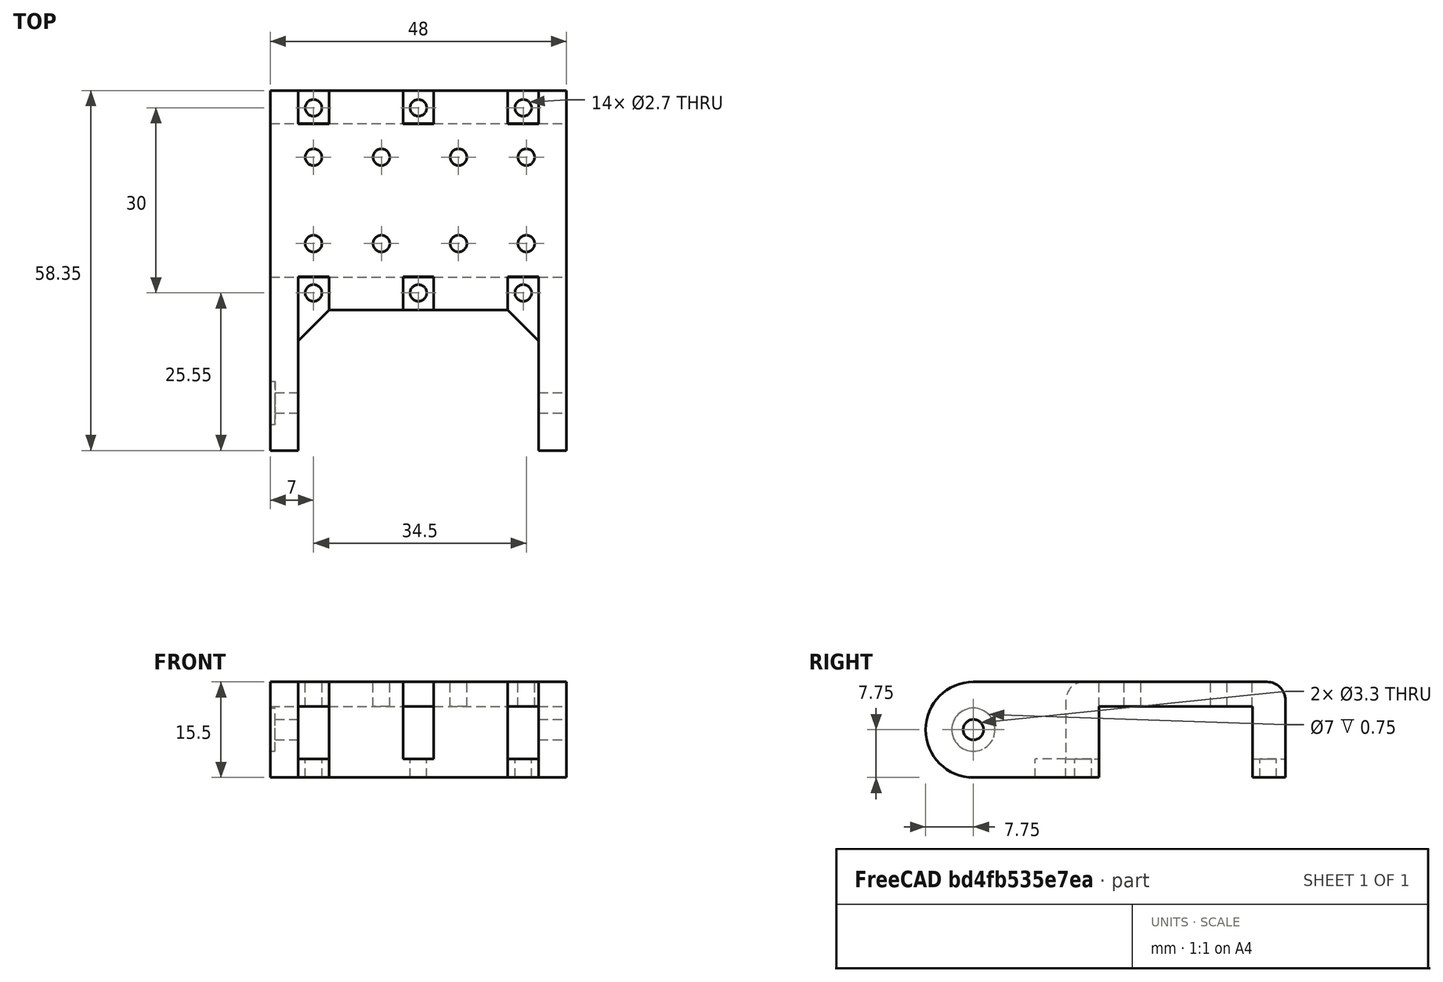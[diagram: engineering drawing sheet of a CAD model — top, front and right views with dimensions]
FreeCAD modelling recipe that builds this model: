
FCSTD DOCUMENT  (FreeCAD 0.15R4671 (Git))
Label: side_mx_28_mount_tendon
License: CC-BY 3.0
LicenseURL: http://creativecommons.org/licenses/by/3.0/
objects: Part::Cylinder×18, Part::MultiFuse×15, Part::Box×11, Part::Cut×3, Part::Fillet×1, Part::Chamfer×1
note: 49 computed .brp shape members not serialized (recipe doc carries the construction recipe); baked Part::Feature solids carry a one-line shape summary decoded from their .brp

FEATURE [Part::Box] Box
  Height = 15.5
  Length = 48.5
  Placement = pos=(-1,0,0) rot=(0,0,1;0rad)
  Width = 35.6
FEATURE [Part::Box] Box001
  Height = 11.5
  Length = 48.5
  Placement = pos=(-1,5.35,0) rot=(0,0,1;0rad)
  Width = 24.9
FEATURE [Part::Cut] Cut
  Base = -> Box
  Tool = -> Box001
FEATURE [Part::Cylinder] Cylinder
  Angle = 360
  Height = 20
  Placement = pos=(6,2.8,0) rot=(0,0,1;0rad)
  Radius = 1.35
FEATURE [Part::Box] Box002
  Height = 20
  Length = 5
  Placement = pos=(3.5,-2.6,3) rot=(0,0,1;0rad)
  Width = 8
FEATURE [Part::MultiFuse] Fusion
  Shapes = -> [Box002,Cylinder]
FEATURE [Part::Fillet] Fillet
  Base = -> Cut
  Edges = 2 edges r=3: [Edge9,Edge11]
FEATURE [Part::Cylinder] Cylinder001
  Angle = 360
  Height = 20
  Placement = pos=(6,2.8,0) rot=(0,0,1;0rad)
  Radius = 1.35
FEATURE [Part::Box] Box003
  Height = 20
  Length = 5
  Placement = pos=(3.5,-2.6,3) rot=(0,0,1;0rad)
  Width = 8
FEATURE [Part::MultiFuse] Fusion001
  Placement = pos=(17,0,0) rot=(0,0,1;0rad)
  Shapes = -> [Box003,Cylinder001]
FEATURE [Part::Cylinder] Cylinder002
  Angle = 360
  Height = 20
  Placement = pos=(6,2.8,0) rot=(0,0,1;0rad)
  Radius = 1.35
FEATURE [Part::Box] Box004
  Height = 20
  Length = 5
  Placement = pos=(3.5,-2.6,3) rot=(0,0,1;0rad)
  Width = 8
FEATURE [Part::MultiFuse] Fusion002
  Placement = pos=(34,0,0) rot=(0,0,1;0rad)
  Shapes = -> [Box004,Cylinder002]
FEATURE [Part::Cylinder] Cylinder003
  Angle = 360
  Height = 20
  Placement = pos=(6,32.8,0) rot=(0,0,1;0rad)
  Radius = 1.35
FEATURE [Part::Box] Box005
  Height = 20
  Length = 5
  Placement = pos=(3.5,30.2,3) rot=(0,0,1;0rad)
  Width = 8
FEATURE [Part::MultiFuse] Fusion003
  Shapes = -> [Cylinder003,Box005]
FEATURE [Part::Box] Box006
  Height = 20
  Length = 5
  Placement = pos=(3.5,30.2,3) rot=(0,0,1;0rad)
  Width = 8
FEATURE [Part::Cylinder] Cylinder004
  Angle = 360
  Height = 20
  Placement = pos=(6,32.8,0) rot=(0,0,1;0rad)
  Radius = 1.35
FEATURE [Part::MultiFuse] Fusion004
  Placement = pos=(17,0,0) rot=(0,0,1;0rad)
  Shapes = -> [Cylinder004,Box006]
FEATURE [Part::Box] Box007
  Height = 20
  Length = 5
  Placement = pos=(3.5,30.2,3) rot=(0,0,1;0rad)
  Width = 8
FEATURE [Part::Cylinder] Cylinder005
  Angle = 360
  Height = 20
  Placement = pos=(6,32.8,0) rot=(0,0,1;0rad)
  Radius = 1.35
FEATURE [Part::MultiFuse] Fusion005
  Placement = pos=(34,0,0) rot=(0,0,1;0rad)
  Shapes = -> [Cylinder005,Box007]
FEATURE [Part::MultiFuse] Fusion006
  Shapes = -> [Fusion005,Fusion004,Fusion002,Fusion003,Fusion001,Fusion]
FEATURE [Part::Cut] Cut001
  Base = -> Fillet
  Tool = -> Fusion006
FEATURE [Part::Cylinder] Cylinder006
  Angle = 360
  Height = 10
  Placement = pos=(6,10.8,9) rot=(0,0,1;0rad)
  Radius = 1.35
FEATURE [Part::Cylinder] Cylinder007
  Angle = 360
  Height = 10
  Placement = pos=(6,24.8,9) rot=(0,0,1;0rad)
  Radius = 1.35
FEATURE [Part::Cylinder] Cylinder008
  Angle = 360
  Height = 10
  Placement = pos=(17,10.8,9) rot=(0,0,1;0rad)
  Radius = 1.35
FEATURE [Part::Cylinder] Cylinder009
  Angle = 360
  Height = 10
  Placement = pos=(17,24.8,9) rot=(0,0,1;0rad)
  Radius = 1.35
FEATURE [Part::MultiFuse] Fusion007
  Shapes = -> [Cylinder009,Cylinder008,Cylinder007,Cylinder006]
FEATURE [Part::Cylinder] Cylinder010
  Angle = 360
  Height = 10
  Placement = pos=(6,10.8,9) rot=(0,0,1;0rad)
  Radius = 1.35
FEATURE [Part::Cylinder] Cylinder011
  Angle = 360
  Height = 10
  Placement = pos=(6,24.8,9) rot=(0,0,1;0rad)
  Radius = 1.35
FEATURE [Part::Cylinder] Cylinder012
  Angle = 360
  Height = 10
  Placement = pos=(17,10.8,9) rot=(0,0,1;0rad)
  Radius = 1.35
FEATURE [Part::Cylinder] Cylinder013
  Angle = 360
  Height = 10
  Placement = pos=(17,24.8,9) rot=(0,0,1;0rad)
  Radius = 1.35
FEATURE [Part::MultiFuse] Fusion008
  Placement = pos=(23.5,0,0) rot=(0,0,1;0rad)
  Shapes = -> [Cylinder013,Cylinder012,Cylinder011,Cylinder010]
FEATURE [Part::MultiFuse] Fusion009
  Shapes = -> [Fusion007,Fusion008]
FEATURE [Part::Box] Box008  label="Cube"
  Height = 15.5
  Length = 4.5
  Placement = pos=(-1,-15,0) rot=(0,0,1;0rad)
  Width = 20
FEATURE [Part::Cylinder] Cylinder014
  Angle = 360
  Height = 4.5
  Placement = pos=(-1,-15,7.75) rot=(0,1,0;1.5708rad)
  Radius = 7.75
FEATURE [Part::MultiFuse] Fusion010
  Shapes = -> [Box008,Cylinder014]
FEATURE [Part::Box] Box009  label="Cube001"
  Height = 15.5
  Length = 4.5
  Placement = pos=(-1,-15,0) rot=(0,0,1;0rad)
  Width = 20
FEATURE [Part::Cylinder] Cylinder015
  Angle = 360
  Height = 4.5
  Placement = pos=(-1,-15,7.75) rot=(0,1,0;1.5708rad)
  Radius = 7.75
FEATURE [Part::MultiFuse] Fusion011
  Placement = pos=(43.5,0,0) rot=(0,0,1;0rad)
  Shapes = -> [Box009,Cylinder015]
FEATURE [Part::Box] Box012  label="Cube004"
  Height = 100
  Length = 10
  Placement = pos=(47,-50,0) rot=(0,0,1;0rad)
  Width = 100
FEATURE [Part::Cylinder] Cylinder018
  Angle = 360
  Height = 100
  Placement = pos=(-4,-15,7.75) rot=(0,1,0;1.5708rad)
  Radius = 1.65
FEATURE [Part::MultiFuse] Fusion012
  Shapes = -> [Fusion010,Cut001,Fusion011]
FEATURE [Part::MultiFuse] Fusion013
  Shapes = -> [Box012,Cylinder018,Fusion009]
FEATURE [Part::Cylinder] Cylinder019
  Angle = 360
  Height = 0.75
  Placement = pos=(-1,-15,7.75) rot=(0,1,0;1.5708rad)
  Radius = 3.5
FEATURE [Part::MultiFuse] Fusion014
  Shapes = -> [Fusion013,Cylinder019]
FEATURE [Part::Cut] Cut002
  Base = -> Fusion012
  Tool = -> Fusion014
FEATURE [Part::Chamfer] Chamfer
  Base = -> Cut002
  Edges = 2 edges r=5: [Edge26,Edge57]
